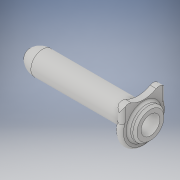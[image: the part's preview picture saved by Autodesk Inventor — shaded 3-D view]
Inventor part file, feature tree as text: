
AUTODESK INVENTOR PART (.ipt)
format: ipt  version: 2018.3 (Build 223284000, 284)  size: 215,040 bytes
history: native  units: in
note: dims shown in document units (in); Inventor stores cm internally (conversion verified against a paired STEP export)
features: sketch x2, extrude x2, revolve x1, plane x1, fillet x1
ambient origin geometry x8: Origin, YZ Plane, XZ Plane, XY Plane, X Axis, Y Axis, Z Axis, Center Point
bodies: Solid1 (feature_tree)
feature tree (7):
  revolve  "Revolution1"  [1 undecoded]
  plane  "Work Plane1"
  sketch  "Sketch2"  dims[d2=0.095in d3=0.224in d4=0.03in d5=0.03in d8=0.168in d9=0.033in d10=0.1in d13=0.187in d14=0.5in d16=0.5in d17=0.033in d18=0.033in d20=90.0deg d21=0.27in d22=0.72in d23=0.312in d24=0.18in d25=1.0in d26=0.0in d27=1.0in d28=0.0in d29=0.044in]
  extrude  "Extrusion1"  Depth=0.044in
  extrude  "Extrusion2"  Depth=0.044in
  fillet  "Fillet1"  Radius=0.03in
  sketch  "Sketch1"  dims[d0=1.745in d1=0.135in]
note: 1 required parameter value undecoded (feature->parameter linkage not recoverable at this tier; creation-order binding heuristic only, values carry confidence <= 0.55)
